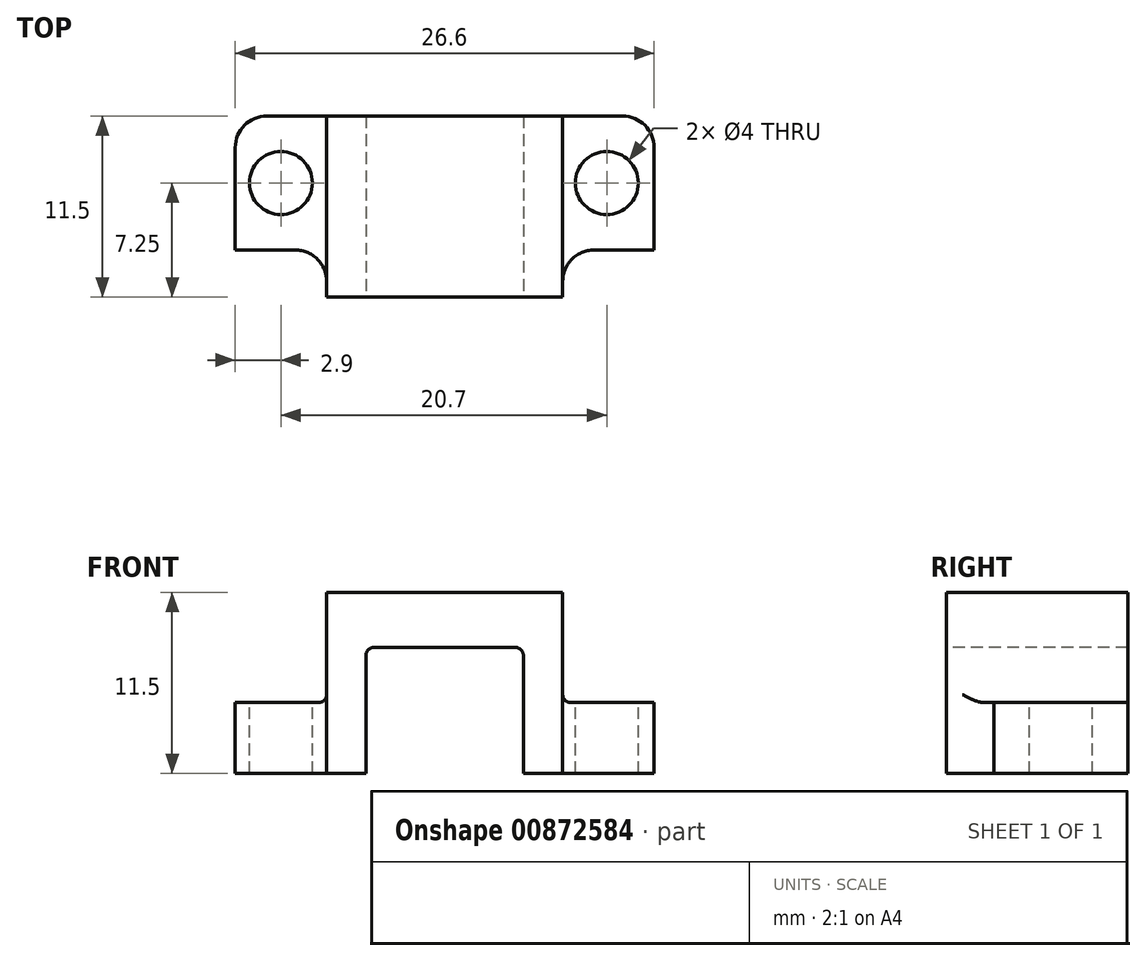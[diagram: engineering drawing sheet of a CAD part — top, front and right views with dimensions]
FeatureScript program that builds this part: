
annotation { "Feature Type Name" : "Feature", "Feature Type Description" : "" }
export const myFeature = defineFeature(function(context is Context, id is Id, definition is map)
    precondition{}
    {
        {
            var Q0;
            Q0=qCreatedBy(makeId("Top.planeOp"),FACE);
            var sketch = newSketch(context, id + "F0", { "sketchPlane" : qUnion([Q0])});
            skLineSegment(sketch, "E0.bottom", {"start": v(-13.3, 5.75) * mm, "end": v(13.3, 5.75) * mm});
            skLineSegment(sketch, "E0.top", {"start": v(-13.3, -5.75) * mm, "end": v(13.3, -5.75) * mm});
            skLineSegment(sketch, "E0.left", {"start": v(-13.3, 5.75) * mm, "end": v(-13.3, -5.75) * mm});
            skLineSegment(sketch, "E0.right", {"start": v(13.3, 5.75) * mm, "end": v(13.3, -5.75) * mm});
            skPoint(sketch, "E1", {"position": v(0, 5.75) * mm});
            skPoint(sketch, "E2", {"position": v(13.3, 0) * mm});
            skSolve(sketch);
        }
        {
            var Q0;
            Q0=qSketchRegion(id+"F0",true);
            extrude(context, id + "F1", {"entities" : qUnion([Q0]), "depth" : 11.5 * mm});
        }
        {
            var Q0;
            Q0=makeQuery(id+"F1.opExtrude","SWEPT_FACE",FACE,{"disambiguationData":[OSD([sQuery(id+"F0.wireOp",EDGE,"E0.top")])]});
            var sketch = newSketch(context, id + "F2", { "sketchPlane" : qUnion([Q0])});
            skLineSegment(sketch, "E3.bottom", {"start": v(-13.3, 11.5) * mm, "end": v(-7.5, 11.5) * mm});
            skLineSegment(sketch, "E3.top", {"start": v(-13.3, 4.5) * mm, "end": v(-7.5, 4.5) * mm});
            skLineSegment(sketch, "E3.left", {"start": v(-13.3, 11.5) * mm, "end": v(-13.3, 4.5) * mm});
            skLineSegment(sketch, "E3.right", {"start": v(-7.5, 11.5) * mm, "end": v(-7.5, 4.5) * mm});
            skLineSegment(sketch, "E4.bottom", {"start": v(13.3, 11.5) * mm, "end": v(7.5, 11.5) * mm});
            skLineSegment(sketch, "E4.top", {"start": v(13.3, 4.5) * mm, "end": v(7.5, 4.5) * mm});
            skLineSegment(sketch, "E4.left", {"start": v(13.3, 11.5) * mm, "end": v(13.3, 4.5) * mm});
            skLineSegment(sketch, "E4.right", {"start": v(7.5, 11.5) * mm, "end": v(7.5, 4.5) * mm});
            skLineSegment(sketch, "E5.bottom", {"start": v(-5, 0) * mm, "end": v(5, 0) * mm});
            skLineSegment(sketch, "E5.top", {"start": v(-5, 8) * mm, "end": v(5, 8) * mm});
            skLineSegment(sketch, "E5.left", {"start": v(-5, 0) * mm, "end": v(-5, 8) * mm});
            skLineSegment(sketch, "E5.right", {"start": v(5, 0) * mm, "end": v(5, 8) * mm});
            skPoint(sketch, "E6", {"position": v(0, 8) * mm});
            skSolve(sketch);
        }
        {
            var Q0;
            Q0=qSketchRegion(id+"F2",true);
            extrude(context, id + "F3", {"entities" : qUnion([Q0]), "operationType" : NewBodyOperationType.REMOVE, "endBound" : BoundingType.THROUGH_ALL, "oppositeDirection" : true, "depth" : 25 * mm});
        }
        {
            var Q0;
            Q0=makeQuery(id+"F3.boolean.opBoolean","COPY",FACE,{"derivedFrom":makeQuery(id+"F3.opExtrude","SWEPT_FACE",FACE,{"disambiguationData":[OSD([sQuery(id+"F2.wireOp",EDGE,"E3.top")])]})});
            var sketch = newSketch(context, id + "F4", { "sketchPlane" : qUnion([Q0])});
            skLineSegment(sketch, "E7.bottom", {"start": v(-13.3, -5.75) * mm, "end": v(-7.5, -5.75) * mm});
            skLineSegment(sketch, "E7.top", {"start": v(-13.3, -2.75) * mm, "end": v(-7.5, -2.75) * mm});
            skLineSegment(sketch, "E7.left", {"start": v(-13.3, -5.75) * mm, "end": v(-13.3, -2.75) * mm});
            skLineSegment(sketch, "E7.right", {"start": v(-7.5, -5.75) * mm, "end": v(-7.5, -2.75) * mm});
            skCircle(sketch, "E8", {"center": v(-10.4, 1.5) * mm, "radius": 2 * mm});
            skPoint(sketch, "E8.centerSnap0", {"position": v(-10.4, 5.75) * mm});
            skSolve(sketch);
        }
        {
            var Q0;
            Q0=qSketchRegion(id+"F4",true);
            extrude(context, id + "F5", {"entities" : qUnion([Q0]), "operationType" : NewBodyOperationType.REMOVE, "endBound" : BoundingType.THROUGH_ALL, "oppositeDirection" : true, "depth" : 25 * mm});
        }
        {
            var Q0;
            Q0=makeQuery(id+"F3.boolean.opBoolean","COPY",FACE,{"derivedFrom":makeQuery(id+"F3.opExtrude","SWEPT_FACE",FACE,{"disambiguationData":[OSD([sQuery(id+"F2.wireOp",EDGE,"E4.top")])]})});
            var sketch = newSketch(context, id + "F6", { "sketchPlane" : qUnion([Q0])});
            skLineSegment(sketch, "E9.bottom", {"start": v(13.3, -5.75) * mm, "end": v(7.5, -5.75) * mm});
            skLineSegment(sketch, "E9.top", {"start": v(13.3, -2.75) * mm, "end": v(7.5, -2.75) * mm});
            skLineSegment(sketch, "E9.left", {"start": v(13.3, -5.75) * mm, "end": v(13.3, -2.75) * mm});
            skLineSegment(sketch, "E9.right", {"start": v(7.5, -5.75) * mm, "end": v(7.5, -2.75) * mm});
            skCircle(sketch, "E10", {"center": v(10.3, 1.5) * mm, "radius": 2 * mm});
            skPoint(sketch, "E11", {"position": v(10.4, 5.75) * mm});
            skSolve(sketch);
        }
        {
            var Q0;
            Q0=qSketchRegion(id+"F6",true);
            extrude(context, id + "F7", {"entities" : qUnion([Q0]), "operationType" : NewBodyOperationType.REMOVE, "endBound" : BoundingType.THROUGH_ALL, "oppositeDirection" : true, "depth" : 25 * mm});
        }
        {
            var Q0;
            Q0=makeQuery(id+"F3.boolean.opBoolean","COPY",EDGE,{"derivedFrom":makeQuery(id+"F3.opExtrude","SWEPT_EDGE",EDGE,{"disambiguationData":[OSD([sQuery(id+"F0.wireOp",EDGE,"E0.top"),sQuery(id+"F2.wireOp",EDGE,"E3.bottom"),sQuery(id+"F2.wireOp",EDGE,"E3.right")])]})});
            var Q1;
            Q1=makeQuery(id+"F3.boolean.opBoolean","COPY",EDGE,{"derivedFrom":makeQuery(id+"F3.opExtrude","SWEPT_EDGE",EDGE,{"disambiguationData":[OSD([sQuery(id+"F0.wireOp",EDGE,"E0.top"),sQuery(id+"F2.wireOp",EDGE,"E4.bottom"),sQuery(id+"F2.wireOp",EDGE,"E4.right")])]})});
            var Q2;
            Q2=makeQuery(id+"F5.boolean.opBoolean","COPY",EDGE,{"derivedFrom":makeQuery(id+"F5.opExtrude","SWEPT_EDGE",EDGE,{"disambiguationData":[OSD([sQuery(id+"F0.wireOp",EDGE,"E0.top"),sQuery(id+"F0.wireOp",EDGE,"E0.left"),sQuery(id+"F2.wireOp",EDGE,"E3.top"),sQuery(id+"F2.wireOp",EDGE,"E3.left"),sQuery(id+"F4.wireOp",EDGE,"E7.top"),sQuery(id+"F4.wireOp",EDGE,"E7.left")])]})});
            var Q3;
            Q3=makeQuery(id+"F1.opExtrude","SWEPT_EDGE",EDGE,{"disambiguationData":[OSD([sQuery(id+"F0.wireOp",EDGE,"E0.bottom"),sQuery(id+"F0.wireOp",EDGE,"E0.left")])]});
            var Q4;
            Q4=makeQuery(id+"F5.boolean.opBoolean","COPY",EDGE,{"derivedFrom":makeQuery(id+"F5.opExtrude","SWEPT_EDGE",EDGE,{"disambiguationData":[OSD([sQuery(id+"F2.wireOp",EDGE,"E3.top"),sQuery(id+"F2.wireOp",EDGE,"E3.right"),sQuery(id+"F4.wireOp",EDGE,"E7.top"),sQuery(id+"F4.wireOp",EDGE,"E7.right")])]})});
            var Q5;
            Q5=makeQuery(id+"F1.opExtrude","SWEPT_EDGE",EDGE,{"disambiguationData":[OSD([sQuery(id+"F0.wireOp",EDGE,"E0.bottom"),sQuery(id+"F0.wireOp",EDGE,"E0.right")])]});
            var Q6;
            Q6=makeQuery(id+"F7.boolean.opBoolean","COPY",EDGE,{"derivedFrom":makeQuery(id+"F7.opExtrude","SWEPT_EDGE",EDGE,{"disambiguationData":[OSD([sQuery(id+"F0.wireOp",EDGE,"E0.top"),sQuery(id+"F0.wireOp",EDGE,"E0.right"),sQuery(id+"F2.wireOp",EDGE,"E4.top"),sQuery(id+"F2.wireOp",EDGE,"E4.left"),sQuery(id+"F6.wireOp",EDGE,"E9.top"),sQuery(id+"F6.wireOp",EDGE,"E9.left")])]})});
            var Q7;
            Q7=makeQuery(id+"F7.boolean.opBoolean","COPY",EDGE,{"derivedFrom":makeQuery(id+"F7.opExtrude","SWEPT_EDGE",EDGE,{"disambiguationData":[OSD([sQuery(id+"F2.wireOp",EDGE,"E4.top"),sQuery(id+"F2.wireOp",EDGE,"E4.right"),sQuery(id+"F6.wireOp",EDGE,"E9.top"),sQuery(id+"F6.wireOp",EDGE,"E9.right")])]})});
            fillet(context, id + "F8", {"entities" : qUnion([Q0, Q1, Q2, Q3, Q4, Q5, Q6, Q7]), "radius" : 2 * mm, "tangentPropagation" : true, "allowEdgeOverflow" : false});
        }
        {
            var Q0;
            Q0=makeQuery(id+"F3.boolean.opBoolean","COPY",EDGE,{"derivedFrom":makeQuery(id+"F3.opExtrude","SWEPT_EDGE",EDGE,{"disambiguationData":[OSD([sQuery(id+"F2.wireOp",EDGE,"E3.top"),sQuery(id+"F2.wireOp",EDGE,"E3.right")])]})});
            var Q1;
            Q1=makeQuery(id+"F3.boolean.opBoolean","COPY",EDGE,{"derivedFrom":makeQuery(id+"F3.opExtrude","SWEPT_EDGE",EDGE,{"disambiguationData":[OSD([sQuery(id+"F2.wireOp",EDGE,"E4.top"),sQuery(id+"F2.wireOp",EDGE,"E4.right")])]})});
            var Q2;
            Q2=makeQuery(id+"F3.boolean.opBoolean","COPY",EDGE,{"derivedFrom":makeQuery(id+"F3.opExtrude","SWEPT_EDGE",EDGE,{"disambiguationData":[OSD([sQuery(id+"F2.wireOp",EDGE,"E5.top"),sQuery(id+"F2.wireOp",EDGE,"E5.left")])]})});
            var Q3;
            Q3=makeQuery(id+"F3.boolean.opBoolean","COPY",EDGE,{"derivedFrom":makeQuery(id+"F3.opExtrude","SWEPT_EDGE",EDGE,{"disambiguationData":[OSD([sQuery(id+"F2.wireOp",EDGE,"E5.top"),sQuery(id+"F2.wireOp",EDGE,"E5.right")])]})});
            fillet(context, id + "F9", {"entities" : qUnion([Q0, Q1, Q2, Q3]), "radius" : 0.5 * mm, "tangentPropagation" : true, "allowEdgeOverflow" : false});
        }
    });
